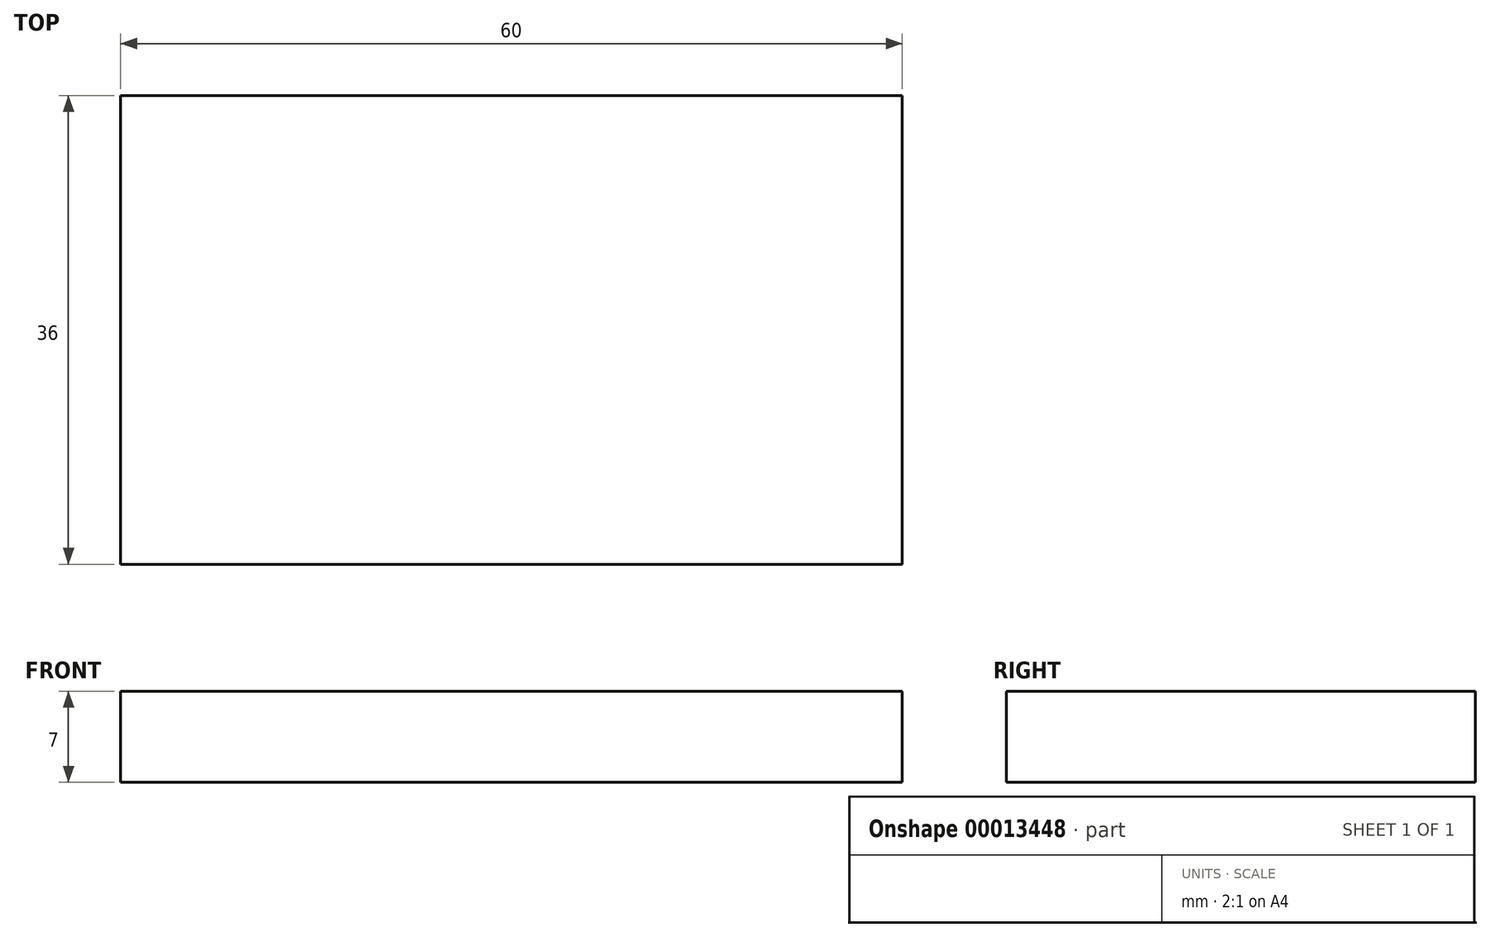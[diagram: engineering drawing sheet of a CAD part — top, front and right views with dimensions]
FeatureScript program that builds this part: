
annotation { "Feature Type Name" : "Feature", "Feature Type Description" : "" }
export const myFeature = defineFeature(function(context is Context, id is Id, definition is map)
    precondition{}
    {
        {
            var Q0;
            Q0=qCreatedBy(makeId("Top.planeOp"),FACE);
            var sketch = newSketch(context, id + "F0", { "sketchPlane" : qUnion([Q0])});
            skLineSegment(sketch, "E0.bottom", {"start": v(-64.73, 36) * mm, "end": v(-4.73, 36) * mm});
            skLineSegment(sketch, "E0.top", {"start": v(-64.73, 0) * mm, "end": v(-4.73, 0) * mm});
            skLineSegment(sketch, "E0.left", {"start": v(-64.73, 36) * mm, "end": v(-64.73, 0) * mm});
            skLineSegment(sketch, "E0.right", {"start": v(-4.73, 36) * mm, "end": v(-4.73, 0) * mm});
            skSolve(sketch);
        }
        {
            var Q0;
            Q0=qSketchRegion(id+"F0",true);
            extrude(context, id + "F1", {"entities" : qUnion([Q0]), "depth" : 7 * mm});
        }
    });
